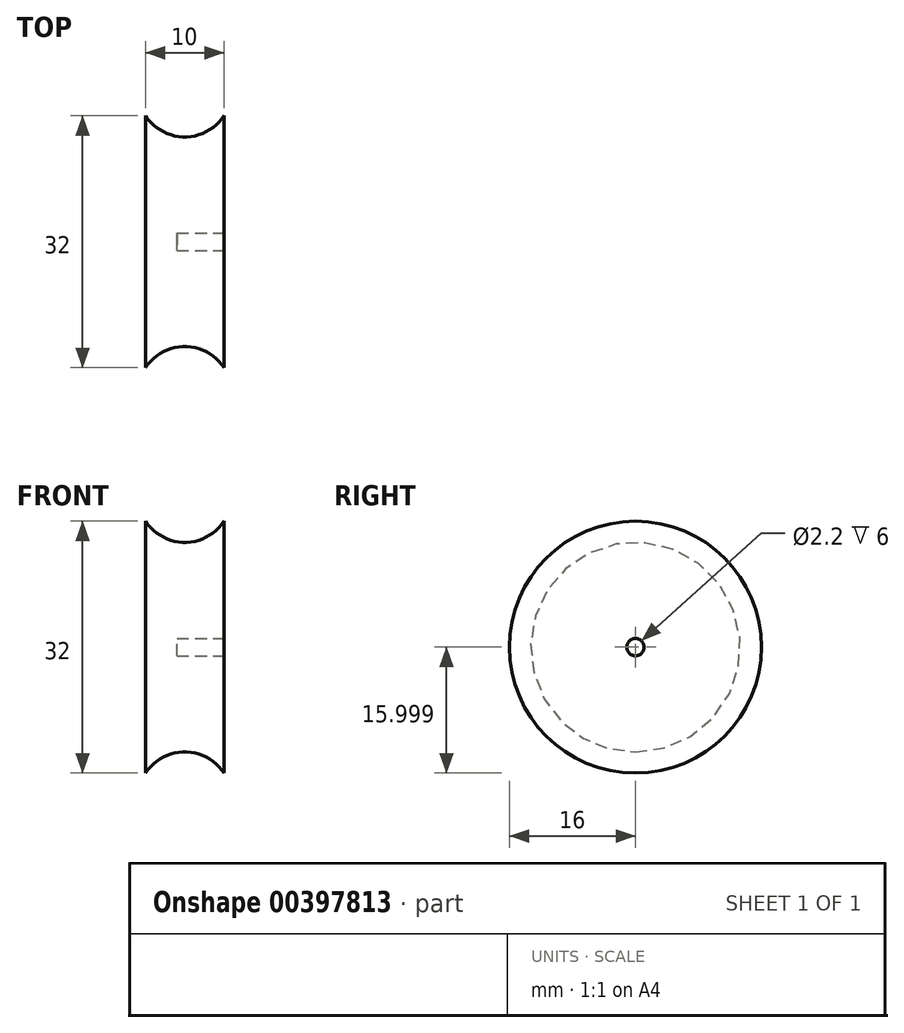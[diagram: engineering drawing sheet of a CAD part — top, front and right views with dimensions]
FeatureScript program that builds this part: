
annotation { "Feature Type Name" : "Feature", "Feature Type Description" : "" }
export const myFeature = defineFeature(function(context is Context, id is Id, definition is map)
    precondition{}
    {
        {
            var Q0;
            Q0=qCreatedBy(makeId("Front.planeOp"),FACE);
            var sketch = newSketch(context, id + "F0", { "sketchPlane" : qUnion([Q0])});
            skArc(sketch, "E0", {"start": v(0.7, 18.06) * mm, "mid": v(-4.3, 20.74) * mm, "end": v(-9.3, 18.06) * mm});
            skLineSegment(sketch, "E1", {"start": v(-5.3, 34.06) * mm, "end": v(-9.3, 34.06) * mm});
            skLineSegment(sketch, "E2", {"start": v(-9.3, 32.96) * mm, "end": v(-9.3, 18.06) * mm});
            skLineSegment(sketch, "E3", {"start": v(0.7, 32.96) * mm, "end": v(0.7, 18.06) * mm});
            skLineSegment(sketch, "E4", {"start": v(-5.3, 32.96) * mm, "end": v(0.7, 32.96) * mm});
            skLineSegment(sketch, "E5", {"start": v(-9.3, 34.06) * mm, "end": v(-9.3, 32.96) * mm});
            skLineSegment(sketch, "E6", {"start": v(-5.3, 34.06) * mm, "end": v(-5.3, 32.96) * mm});
            skPoint(sketch, "E7.end.orphan", {"position": v(0.7, 34.06) * mm});
            skSolve(sketch);
        }
        {
            var Q0;
            Q0 = qSketchRegion(id + "F0", true);
            var Q1;
            Q1=sQuery(id+"F0.wireOp",EDGE,"E1");
            revolve(context, id + "F1", {"entities" : qUnion([Q0]), "axis" : qUnion([Q1]), "revolveType" : RevolveType.FULL});
        }
    });
